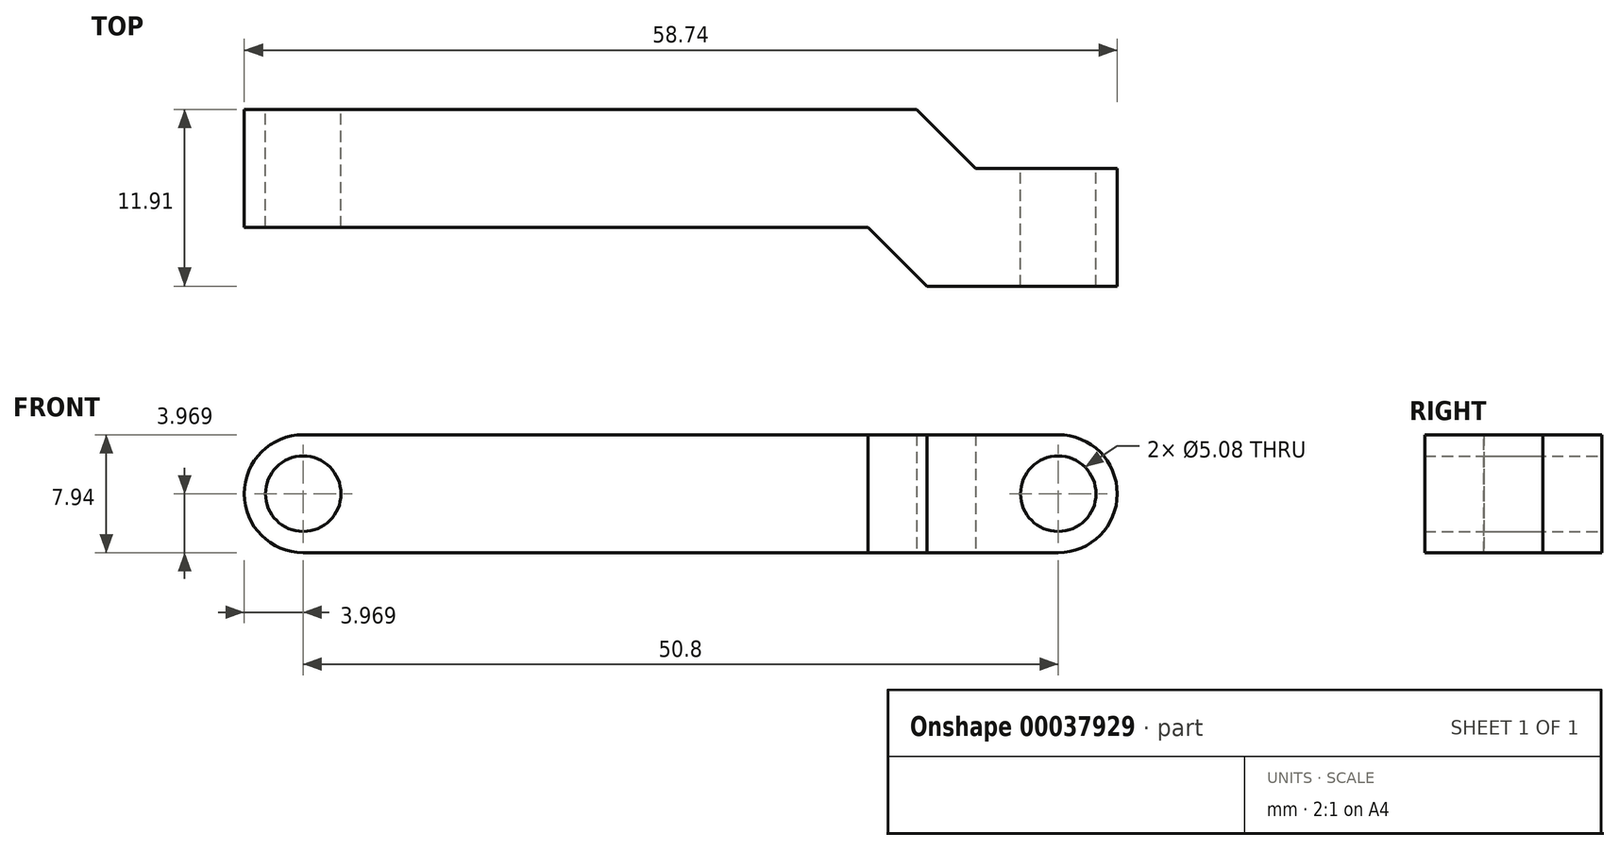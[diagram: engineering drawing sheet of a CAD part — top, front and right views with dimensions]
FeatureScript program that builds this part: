
annotation { "Feature Type Name" : "Feature", "Feature Type Description" : "" }
export const myFeature = defineFeature(function(context is Context, id is Id, definition is map)
    precondition{}
    {
        {
            var Q0;
            Q0=qCreatedBy(makeId("Top.planeOp"),FACE);
            var sketch = newSketch(context, id + "F0", { "sketchPlane" : qUnion([Q0])});
            skLineSegment(sketch, "E0.bottom", {"start": v(0, 0) * mm, "end": v(45.24, 0) * mm});
            skLineSegment(sketch, "E0.top", {"start": v(0, -7.94) * mm, "end": v(41.96, -7.94) * mm});
            skLineSegment(sketch, "E0.left", {"start": v(0, 0) * mm, "end": v(0, -7.94) * mm});
            skLineSegment(sketch, "E1", {"start": v(41.96, -7.94) * mm, "end": v(45.92, -11.9) * mm});
            skLineSegment(sketch, "E2", {"start": v(45.24, 0) * mm, "end": v(49.21, -3.97) * mm});
            skLineSegment(sketch, "E3", {"start": v(49.21, -3.97) * mm, "end": v(58.74, -3.97) * mm});
            skLineSegment(sketch, "E4", {"start": v(58.74, -3.97) * mm, "end": v(58.74, -11.9) * mm});
            skLineSegment(sketch, "E5", {"start": v(45.24, 0) * mm, "end": v(58.74, 0) * mm, "construction": true});
            skLineSegment(sketch, "E6", {"start": v(58.74, 0) * mm, "end": v(58.74, -3.97) * mm, "construction": true});
            skLineSegment(sketch, "E7", {"start": v(47.23, -1.98) * mm, "end": v(41.62, -7.6) * mm, "construction": true});
            skLineSegment(sketch, "E8", {"start": v(45.92, -11.9) * mm, "end": v(58.74, -11.9) * mm});
            skLineSegment(sketch, "E9", {"start": v(41.96, -7.94) * mm, "end": v(41.62, -7.6) * mm, "construction": true});
            skSolve(sketch);
        }
        {
            var Q0;
            Q0 = qSketchRegion(id + "F0", true);
            extrude(context, id + "F1", {"entities" : qUnion([Q0]), "depth" : 7.94 * mm});
        }
        {
            var Q0;
            Q0=makeQuery(id+"F1.opExtrude","CAP_EDGE",EDGE,{"disambiguationData":[OSD([sQuery(id+"F0.wireOp",EDGE,"E0.left")])],"isStart":true});
            var Q1;
            Q1=makeQuery(id+"F1.opExtrude","CAP_EDGE",EDGE,{"disambiguationData":[OSD([sQuery(id+"F0.wireOp",EDGE,"E0.left")])],"isStart":false});
            var Q2;
            Q2=makeQuery(id+"F1.opExtrude","CAP_EDGE",EDGE,{"disambiguationData":[OSD([sQuery(id+"F0.wireOp",EDGE,"E4")])],"isStart":true});
            var Q3;
            Q3=makeQuery(id+"F1.opExtrude","CAP_EDGE",EDGE,{"disambiguationData":[OSD([sQuery(id+"F0.wireOp",EDGE,"E4")])],"isStart":false});
            fillet(context, id + "F2", {"entities" : qUnion([Q0, Q1, Q2, Q3]), "radius" : 3.97 * mm, "tangentPropagation" : true, "allowEdgeOverflow" : false});
        }
        {
            var Q0;
            Q0=makeQuery(id+"F1.opExtrude","SWEPT_FACE",FACE,{"disambiguationData":[OSD([sQuery(id+"F0.wireOp",EDGE,"E0.bottom")])]});
            var sketch = newSketch(context, id + "F3", { "sketchPlane" : qUnion([Q0])});
            skCircle(sketch, "E10", {"center": v(-3.97, 3.97) * mm, "radius": 2.54 * mm});
            skCircle(sketch, "E11", {"center": v(-54.77, 3.97) * mm, "radius": 2.54 * mm});
            skSolve(sketch);
        }
        {
            var Q0;
            Q0 = qSketchRegion(id + "F3", true);
            var Q1;
            Q1=makeQuery(id+"F1.opExtrude","SWEPT_FACE",FACE,{"disambiguationData":[OSD([sQuery(id+"F0.wireOp",EDGE,"E8")])]});
            extrude(context, id + "F4", {"entities" : qUnion([Q0]), "operationType" : NewBodyOperationType.REMOVE, "endBound" : BoundingType.UP_TO_SURFACE, "oppositeDirection" : true, "endBoundEntityFace" : qUnion([Q1]), "depth" : 25.4 * mm});
        }
    });
